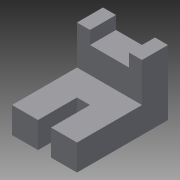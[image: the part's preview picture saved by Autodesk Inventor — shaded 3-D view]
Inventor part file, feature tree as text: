
AUTODESK INVENTOR PART (.ipt)
format: ipt  version: 2015 (Build 190159000, 159)  size: 94,208 bytes
history: native  units: in
note: dims shown in document units (in); Inventor stores cm internally (conversion verified against a paired STEP export)
features: extrude x3, sketch x3
ambient origin geometry x8: Origin, YZ Plane, XZ Plane, XY Plane, X Axis, Y Axis, Z Axis, Center Point
bodies: Solid1 (feature_tree)
feature tree (6):
  extrude  "Extrusion1"  Depth=1.0in
  extrude  "Extrusion2"  Depth=2.5in
  extrude  "Extrusion3"  Depth=0.5in
  sketch  "Sketch1"  dims[d0=1.0in d1=1.0in]
  sketch  "Sketch2"  dims[d2=3.5in d3=2.5in]
  sketch  "Sketch3"  dims[d4=2.5in d5=0.0in d6=0.5in d7=1.5in d8=1.5625in d9=0.0in d10=1.0in d11=0.5in d12=1.5in d13=0.0in]
